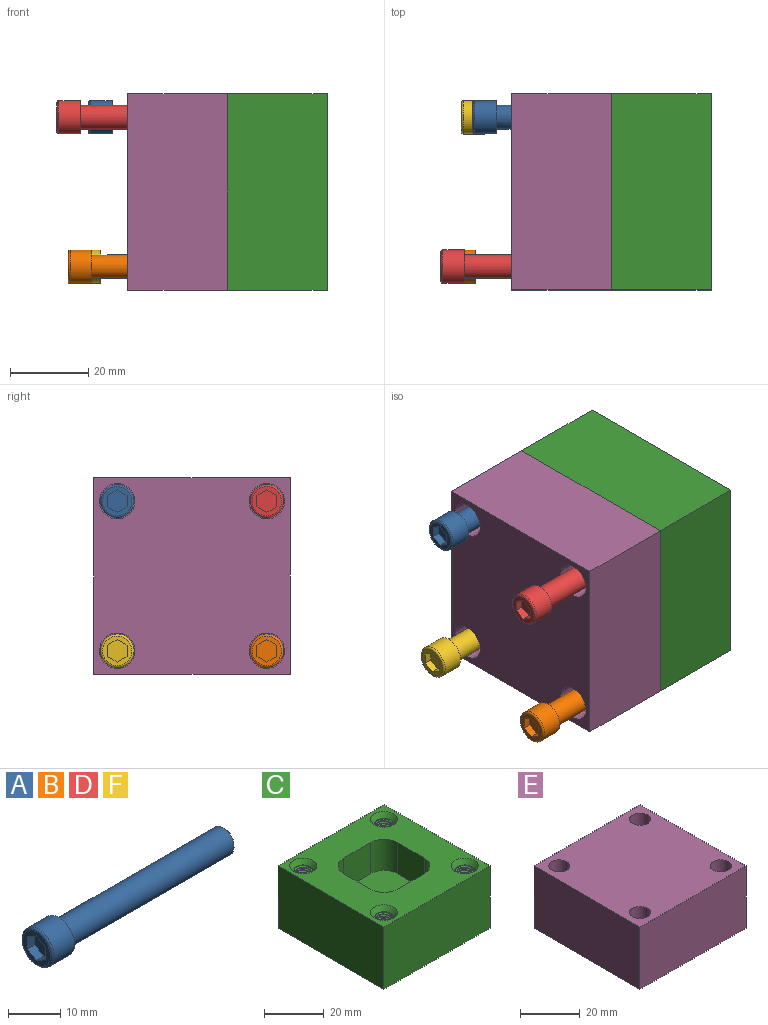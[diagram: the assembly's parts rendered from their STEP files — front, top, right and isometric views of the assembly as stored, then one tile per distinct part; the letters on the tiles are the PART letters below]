
ASSEMBLY  parts=6 mates=5
PART A: 14 faces, bbox 51x9.2x9.2 mm
  f0: plane 7.5x7.5mm, normal (-1,0,0), area 22.5mm2, adj f5,f6,f7,f8,f9,f10,f13
  f1: plane 5x5mm, normal (1,0,0), area 19.6mm2, adj f12
  f2: cylinder r=3mm len=44.5mm, axis (1,0,0), area 838.8mm2, adj f3,f12
  f3: plane 8.5x8.5mm, normal (1,0,0), area 28.5mm2, adj f2,f4
  f4: cylinder r=4.25mm len=8.5mm, axis (1,0,0), area 146.9mm2, adj f3,f13
  f5: plane 2.89x2mm, normal (0,-1,0), area 5.8mm2, adj f0,f6,f10,f11
  f6: plane 2.5x2mm, normal (0,-0.5,0.87), area 5.8mm2, adj f0,f5,f7,f11
  f7: plane 2.5x2mm, normal (0,0.5,0.87), area 5.8mm2, adj f0,f6,f8,f11
  f8: plane 2.89x2mm, normal (0,1,0), area 5.8mm2, adj f0,f7,f9,f11
  f9: plane 2.5x2mm, normal (0,0.5,-0.87), area 5.8mm2, adj f0,f8,f10,f11
  f10: plane 2.5x2mm, normal (0,-0.5,-0.87), area 5.8mm2, adj f0,f5,f9,f11
  f11: plane 5.77x5mm, normal (-1,0,0), area 21.7mm2, adj f5,f6,f7,f8,f9,f10
  f12: cone r=2.5mm half-angle=45deg, axis (-1,0,0), area 12.2mm2, adj f1,f2
  f13: torus R=3.75mm, axis (1,0,0), area 20.1mm2, adj f0,f4
PART B: same geometry as A
PART C: 43 faces, bbox 50.3x50.3x26.2 mm
  f0: plane 50.29x50.29mm, normal (0,0,-1), area 2405.2mm2, adj f1,f2,f3,f4,f19,f20,f21,f24
  f1: plane 50x25.4mm, normal (0,-1,0), area 1270mm2, adj f0,f2,f4,f5
  f2: plane 50x25.4mm, normal (1,0,0), area 1270mm2, adj f0,f1,f3,f5
  f3: plane 50x25.4mm, normal (0,1,0), area 1270mm2, adj f0,f2,f4,f5
  f4: plane 50x25.4mm, normal (-1,0,0), area 1270mm2, adj f0,f1,f3,f5
  f5: plane 50x50mm, normal (0,0,1), area 1635mm2, adj f1,f2,f3,f4,f6,f7,f8,f9
  f6: plane 12.7x12.7mm, normal (-1,0,0), area 161.3mm2, adj f5,f7,f13,f14
  f7: cylinder r=6.35mm len=12.7mm, axis (0,0,1), area 126.7mm2, adj f5,f6,f8,f14
  f8: plane 12.7x12.7mm, normal (0,-1,0), area 161.3mm2, adj f5,f7,f9,f14
  f9: cylinder r=6.35mm len=12.7mm, axis (0,0,1), area 126.7mm2, adj f5,f8,f10,f14
  f10: plane 12.7x12.7mm, normal (1,0,0), area 161.3mm2, adj f5,f9,f11,f14
  f11: cylinder r=6.35mm len=12.7mm, axis (0,0,1), area 126.7mm2, adj f5,f10,f12,f14
  f12: plane 12.7x12.7mm, normal (0,1,0), area 161.3mm2, adj f5,f11,f13,f14
  f13: cylinder r=6.35mm len=12.7mm, axis (0,0,1), area 126.7mm2, adj f5,f6,f12,f14
  f14: plane 25.4x25.4mm, normal (0,0,1), area 610.5mm2, adj f6,f7,f8,f9,f10,f11,f12,f13
  f15: cone r=3mm half-angle=41deg, axis (0,0,1), area 53.9mm2, adj f5,f28,f29
  f16: cone r=3mm half-angle=41deg, axis (0,0,1), area 53.9mm2, adj f5,f34,f35
  f17: cone r=3mm half-angle=41deg, axis (0,0,1), area 53.9mm2, adj f5,f40,f41
  f18: cone r=3mm half-angle=41deg, axis (0,0,1), area 53.9mm2, adj f5,f22,f23
  f19: bspline ~24.48x7.02mm, area 258.5mm2, adj f0,f21,f22,f23,f24
  f20: bspline ~24.48x7.02mm, area 257.5mm2, adj f0,f21,f22,f23,f24
  f21: bspline ~24.13x7.13mm, area 66mm2, adj f0,f19,f20,f22
  f22: plane 2.26x2.22mm, normal (0,0,-1), area 0.2mm2, adj f18,f19,f20,f21
  f23: plane 6.24x6.24mm, normal (0,0,1), area 4.7mm2, adj f18,f19,f20,f24
  f24: cylinder r=2.5mm len=23.67mm, axis (0,0,-1), area 62mm2, adj f0,f19,f20,f23
  f25: bspline ~24.48x7.02mm, area 258.5mm2, adj f0,f27,f28,f29,f30
  f26: bspline ~24.48x7.02mm, area 257.5mm2, adj f0,f27,f28,f29,f30
  f27: bspline ~24.13x7.13mm, area 66mm2, adj f0,f25,f26,f28
  f28: plane 2.26x2.22mm, normal (0,0,-1), area 0.2mm2, adj f15,f25,f26,f27
  f29: plane 6.24x6.24mm, normal (0,0,1), area 4.7mm2, adj f15,f25,f26,f30
  f30: cylinder r=2.5mm len=23.67mm, axis (0,0,-1), area 62mm2, adj f0,f25,f26,f29
  f31: bspline ~24.48x7.02mm, area 258.5mm2, adj f0,f33,f34,f35,f36
  f32: bspline ~24.48x7.02mm, area 257.5mm2, adj f0,f33,f34,f35,f36
  f33: bspline ~24.13x7.13mm, area 66mm2, adj f0,f31,f32,f34
  f34: plane 2.26x2.22mm, normal (0,0,-1), area 0.2mm2, adj f16,f31,f32,f33
  f35: plane 6.24x6.24mm, normal (0,0,1), area 4.7mm2, adj f16,f31,f32,f36
  f36: cylinder r=2.5mm len=23.67mm, axis (0,0,-1), area 62mm2, adj f0,f31,f32,f35
  f37: bspline ~24.48x7.02mm, area 258.5mm2, adj f0,f39,f40,f41,f42
  f38: bspline ~24.48x7.02mm, area 257.5mm2, adj f0,f39,f40,f41,f42
  f39: bspline ~24.13x7.13mm, area 66mm2, adj f0,f37,f38,f40
  f40: plane 2.26x2.22mm, normal (0,0,-1), area 0.2mm2, adj f17,f37,f38,f39
  f41: plane 6.24x6.24mm, normal (0,0,1), area 4.7mm2, adj f17,f37,f38,f42
  f42: cylinder r=2.5mm len=23.67mm, axis (0,0,-1), area 62mm2, adj f0,f37,f38,f41
PART D: same geometry as A
PART E: 18 faces, bbox 50x50x25.4 mm
  f0: plane 50x25.4mm, normal (0,-1,0), area 1270mm2, adj f1,f3,f4,f5
  f1: plane 50x25.4mm, normal (1,0,0), area 1270mm2, adj f0,f2,f4,f5
  f2: plane 50x25.4mm, normal (0,1,0), area 1270mm2, adj f1,f3,f4,f5
  f3: plane 50x25.4mm, normal (-1,0,0), area 1270mm2, adj f0,f2,f4,f5
  f4: plane 50x50mm, normal (0,0,1), area 2346.1mm2, adj f0,f1,f2,f3,f6,f7,f8,f9
  f5: plane 50x50mm, normal (0,0,-1), area 2245.5mm2, adj f0,f1,f2,f3,f10,f12,f14,f16
  f6: cylinder r=3.5mm len=19.4mm, axis (0,0,-1), area 426.6mm2, adj f4,f17
  f7: cylinder r=3.5mm len=19.4mm, axis (0,0,-1), area 426.6mm2, adj f4,f15
  f8: cylinder r=3.5mm len=19.4mm, axis (0,0,-1), area 426.6mm2, adj f4,f13
  f9: cylinder r=3.5mm len=19.4mm, axis (0,0,-1), area 426.6mm2, adj f4,f11
  f10: cylinder r=4.5mm len=9mm, axis (0,0,-1), area 169.6mm2, adj f5,f11
  f11: plane 9x9mm, normal (0,0,-1), area 25.1mm2, adj f9,f10
  f12: cylinder r=4.5mm len=9mm, axis (0,0,-1), area 169.6mm2, adj f5,f13
  f13: plane 9x9mm, normal (0,0,-1), area 25.1mm2, adj f8,f12
  f14: cylinder r=4.5mm len=9mm, axis (0,0,-1), area 169.6mm2, adj f5,f15
  f15: plane 9x9mm, normal (0,0,-1), area 25.1mm2, adj f7,f14
  f16: cylinder r=4.5mm len=9mm, axis (0,0,-1), area 169.6mm2, adj f5,f17
  f17: plane 9x9mm, normal (0,0,-1), area 25.1mm2, adj f6,f16
PART F: same geometry as A
PLACE A rot(axis=(0.99,-0.13,0.07),0deg) t=(-16.79,-13.05,149.35)mm
PLACE B rot(axis=(0.99,-0.13,0.07),0deg) t=(-22.01,-51.15,111.25)mm
PLACE C rot(axis=(-0.71,0,0.71),180deg) t=(18.58,-32.1,130.3)mm fixed
PLACE D rot(axis=(0.99,-0.13,0.07),0deg) t=(-24.88,-51.15,149.35)mm
PLACE E rot(axis=(0,1,0),90deg) t=(-6.82,-32.1,130.3)mm
PLACE F rot(axis=(0.99,-0.13,0.07),0deg) t=(-19.66,-13.05,111.25)mm
MATE slider E.f8 <-> D.f2  axis (-1,0,0) through (-0.82,-51.15,149.35)mm
MATE slider E.f6 <-> F.f2  axis (-1,0,0) through (-0.82,-13.05,111.25)mm
MATE slider E.f4 <-> C.f5  axis (-1,0,0) through (18.58,-7.1,105.3)mm
MATE slider E.f9 <-> B.f2  axis (-1,0,0) through (-0.82,-51.15,111.25)mm
MATE slider E.f7 <-> A.f2  axis (-1,0,0) through (-0.82,-13.05,149.35)mm
